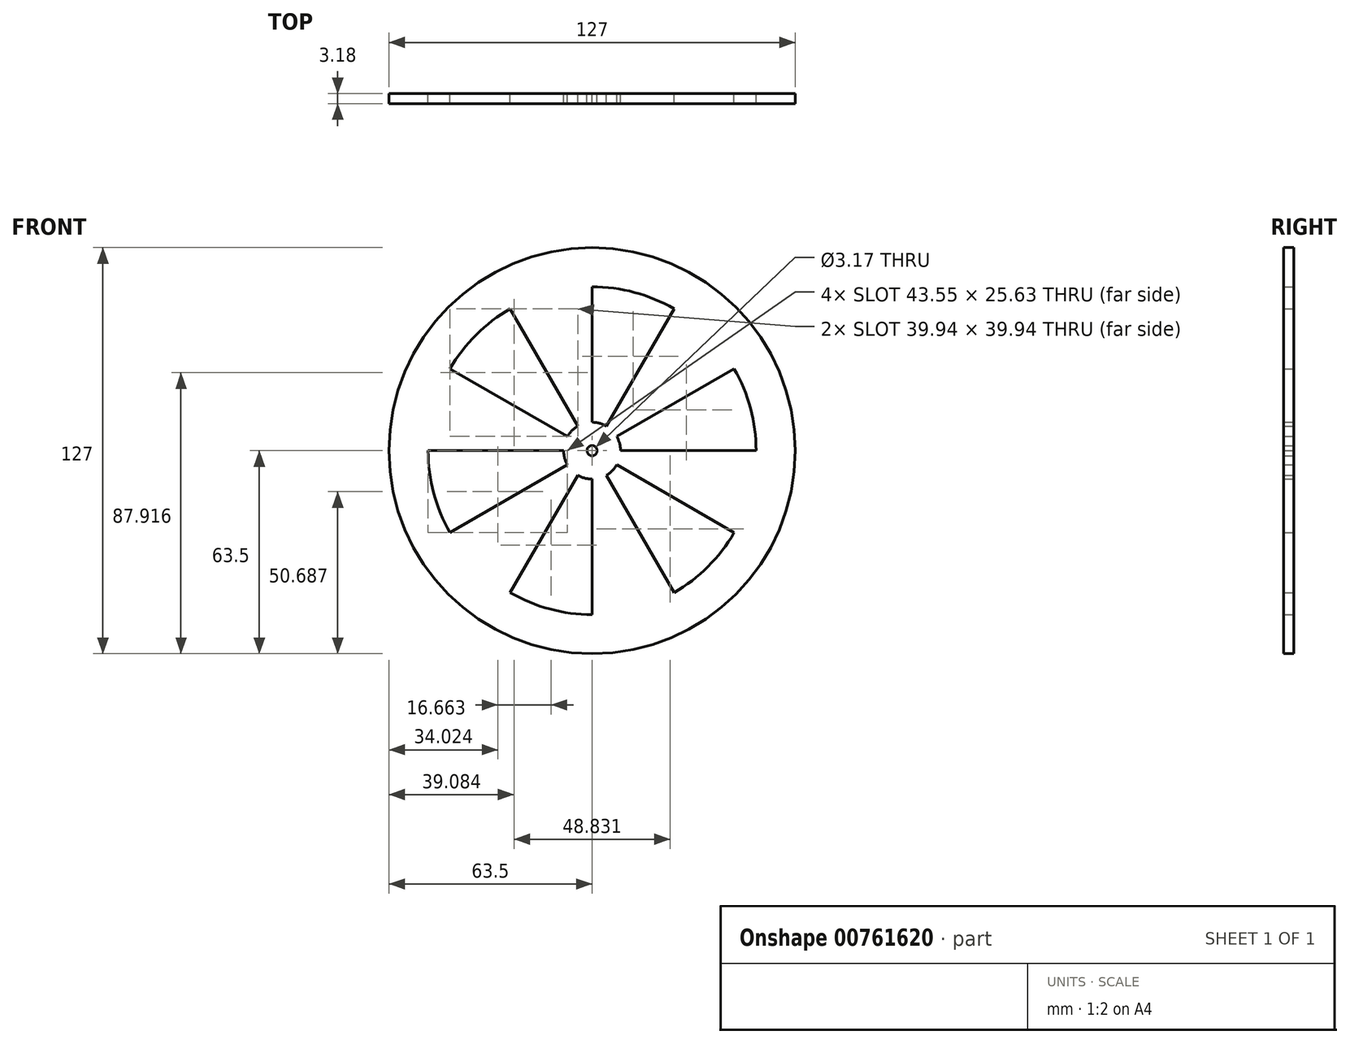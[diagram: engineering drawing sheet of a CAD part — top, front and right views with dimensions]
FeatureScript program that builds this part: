
annotation { "Feature Type Name" : "Feature", "Feature Type Description" : "" }
export const myFeature = defineFeature(function(context is Context, id is Id, definition is map)
    precondition{}
    {
        {
            var Q0;
            Q0=qCreatedBy(makeId("Front.planeOp"),FACE);
            var sketch = newSketch(context, id + "F0", { "sketchPlane" : qUnion([Q0])});
            skCircle(sketch, "E0", {"center": v(0, 0) * mm, "radius": 63.5 * mm});
            skCircle(sketch, "E1", {"center": v(0, 0) * mm, "radius": 51.25 * mm});
            skCircle(sketch, "E2", {"center": v(0, 0) * mm, "radius": 1.59 * mm});
            skCircle(sketch, "E3", {"center": v(0, 0) * mm, "radius": 8.9 * mm});
            skLineSegment(sketch, "E4", {"start": v(-8.89, 0) * mm, "end": v(-51.25, 0) * mm});
            skLineSegment(sketch, "E5.1.0", {"start": v(-7.7, -4.45) * mm, "end": v(-44.39, -25.63) * mm});
            skLineSegment(sketch, "E5.2.0", {"start": v(-4.45, -7.7) * mm, "end": v(-25.63, -44.39) * mm});
            skLineSegment(sketch, "E6.2.3.0", {"start": v(0, -8.9) * mm, "end": v(0, -51.25) * mm});
            skLineSegment(sketch, "E6.2.4.0", {"start": v(4.45, -7.7) * mm, "end": v(25.63, -44.39) * mm});
            skLineSegment(sketch, "E6.2.5.0", {"start": v(7.7, -4.45) * mm, "end": v(44.39, -25.63) * mm});
            skLineSegment(sketch, "E6.2.6.0", {"start": v(8.9, 0) * mm, "end": v(51.25, 0) * mm});
            skLineSegment(sketch, "E6.2.7.0", {"start": v(7.7, 4.45) * mm, "end": v(44.39, 25.63) * mm});
            skLineSegment(sketch, "E6.2.8.0", {"start": v(4.45, 7.7) * mm, "end": v(25.63, 44.39) * mm});
            skLineSegment(sketch, "E6.2.9.0", {"start": v(0, 8.89) * mm, "end": v(0, 51.25) * mm});
            skLineSegment(sketch, "E6.2.10.0", {"start": v(-4.44, 7.7) * mm, "end": v(-25.63, 44.39) * mm});
            skLineSegment(sketch, "E6.2.11.0", {"start": v(-7.7, 4.44) * mm, "end": v(-44.39, 25.63) * mm});
            skSolve(sketch);
        }
        {
            var Q0;
            Q0=makeQuery(id+"F0.imprint","IMPRINT",FACE,{"disambiguationData":[TD([[makeQuery(id+"F0.imprint","IMPRINT",EDGE,{"derivedFrom":sQuery(id+"F0.wireOp",EDGE,"E0")}),1.0]])]});
            var Q1;
            {var subQ0=sQuery(id+"F0.wireOp",EDGE,"E4");Q1=makeQuery(id+"F0.imprint","IMPRINT",FACE,{"disambiguationData":[TD([[makeQuery(id+"F0.imprint","IMPRINT",EDGE,{"derivedFrom":subQ0}),-1.0]])]});}
            var Q2;
            {var subQ0=sQuery(id+"F0.wireOp",EDGE,"E6.2.9.0");Q2=makeQuery(id+"F0.imprint","IMPRINT",FACE,{"disambiguationData":[TD([[makeQuery(id+"F0.imprint","IMPRINT",EDGE,{"derivedFrom":subQ0}),1.0]])]});}
            var Q3;
            {var subQ0=sQuery(id+"F0.wireOp",EDGE,"E6.2.7.0");Q3=makeQuery(id+"F0.imprint","IMPRINT",FACE,{"disambiguationData":[TD([[makeQuery(id+"F0.imprint","IMPRINT",EDGE,{"derivedFrom":subQ0}),1.0]])]});}
            var Q4;
            {var subQ0=sQuery(id+"F0.wireOp",EDGE,"E6.2.5.0");Q4=makeQuery(id+"F0.imprint","IMPRINT",FACE,{"disambiguationData":[TD([[makeQuery(id+"F0.imprint","IMPRINT",EDGE,{"derivedFrom":subQ0}),1.0]])]});}
            var Q5;
            {var subQ0=sQuery(id+"F0.wireOp",EDGE,"E6.2.3.0");Q5=makeQuery(id+"F0.imprint","IMPRINT",FACE,{"disambiguationData":[TD([[makeQuery(id+"F0.imprint","IMPRINT",EDGE,{"derivedFrom":subQ0}),1.0]])]});}
            var Q6;
            {var subQ0=sQuery(id+"F0.wireOp",EDGE,"E5.1.0");Q6=makeQuery(id+"F0.imprint","IMPRINT",FACE,{"disambiguationData":[TD([[makeQuery(id+"F0.imprint","IMPRINT",EDGE,{"derivedFrom":subQ0}),1.0]])]});}
            var Q7;
            Q7=makeQuery(id+"F0.imprint","IMPRINT",FACE,{"disambiguationData":[TD([[makeQuery(id+"F0.imprint","IMPRINT",EDGE,{"derivedFrom":sQuery(id+"F0.wireOp",EDGE,"E2")}),-1.0]])]});
            extrude(context, id + "F1", {"entities" : qUnion([Q0, Q1, Q2, Q3, Q4, Q5, Q6, Q7]), "depth" : 3.17 * mm, "offsetDistance" : 25.4 * mm});
        }
        {
            var Q0;
            Q0=makeQuery(id+"F1.opExtrude","CAP_FACE",FACE,{"disambiguationData":[OSD([sQuery(id+"F0.wireOp",EDGE,"E4"),sQuery(id+"F0.wireOp",EDGE,"E5.1.0"),sQuery(id+"F0.wireOp",EDGE,"E5.2.0"),sQuery(id+"F0.wireOp",EDGE,"E6.2.3.0"),sQuery(id+"F0.wireOp",EDGE,"E6.2.4.0"),sQuery(id+"F0.wireOp",EDGE,"E6.2.5.0"),sQuery(id+"F0.wireOp",EDGE,"E6.2.6.0"),sQuery(id+"F0.wireOp",EDGE,"E6.2.7.0"),sQuery(id+"F0.wireOp",EDGE,"E6.2.8.0"),sQuery(id+"F0.wireOp",EDGE,"E6.2.9.0"),sQuery(id+"F0.wireOp",EDGE,"E6.2.10.0"),sQuery(id+"F0.wireOp",EDGE,"E6.2.11.0"),sQuery(id+"F0.wireOp",EDGE,"E1"),sQuery(id+"F0.wireOp",EDGE,"E3"),sQuery(id+"F0.wireOp",EDGE,"E0"),sQuery(id+"F0.wireOp",EDGE,"E2")])],"isStart":false});
            var sketch = newSketch(context, id + "F2", { "sketchPlane" : qUnion([Q0])});
            skCircle(sketch, "E7", {"center": v(0, 0) * mm, "radius": 1.59 * mm});
            skSolve(sketch);
        }
        {
            var Q0;
            Q0=makeQuery(id+"F2.imprint","IMPRINT",FACE,{"disambiguationData":[TD([[makeQuery(id+"F2.imprint","IMPRINT",EDGE,{"derivedFrom":sQuery(id+"F2.wireOp",EDGE,"E7")}),1.0]])]});
            extrude(context, id + "F3", {"entities" : qUnion([Q0]), "operationType" : NewBodyOperationType.REMOVE, "oppositeDirection" : true, "depth" : 3.17 * mm, "offsetDistance" : 25.4 * mm});
        }
    });
